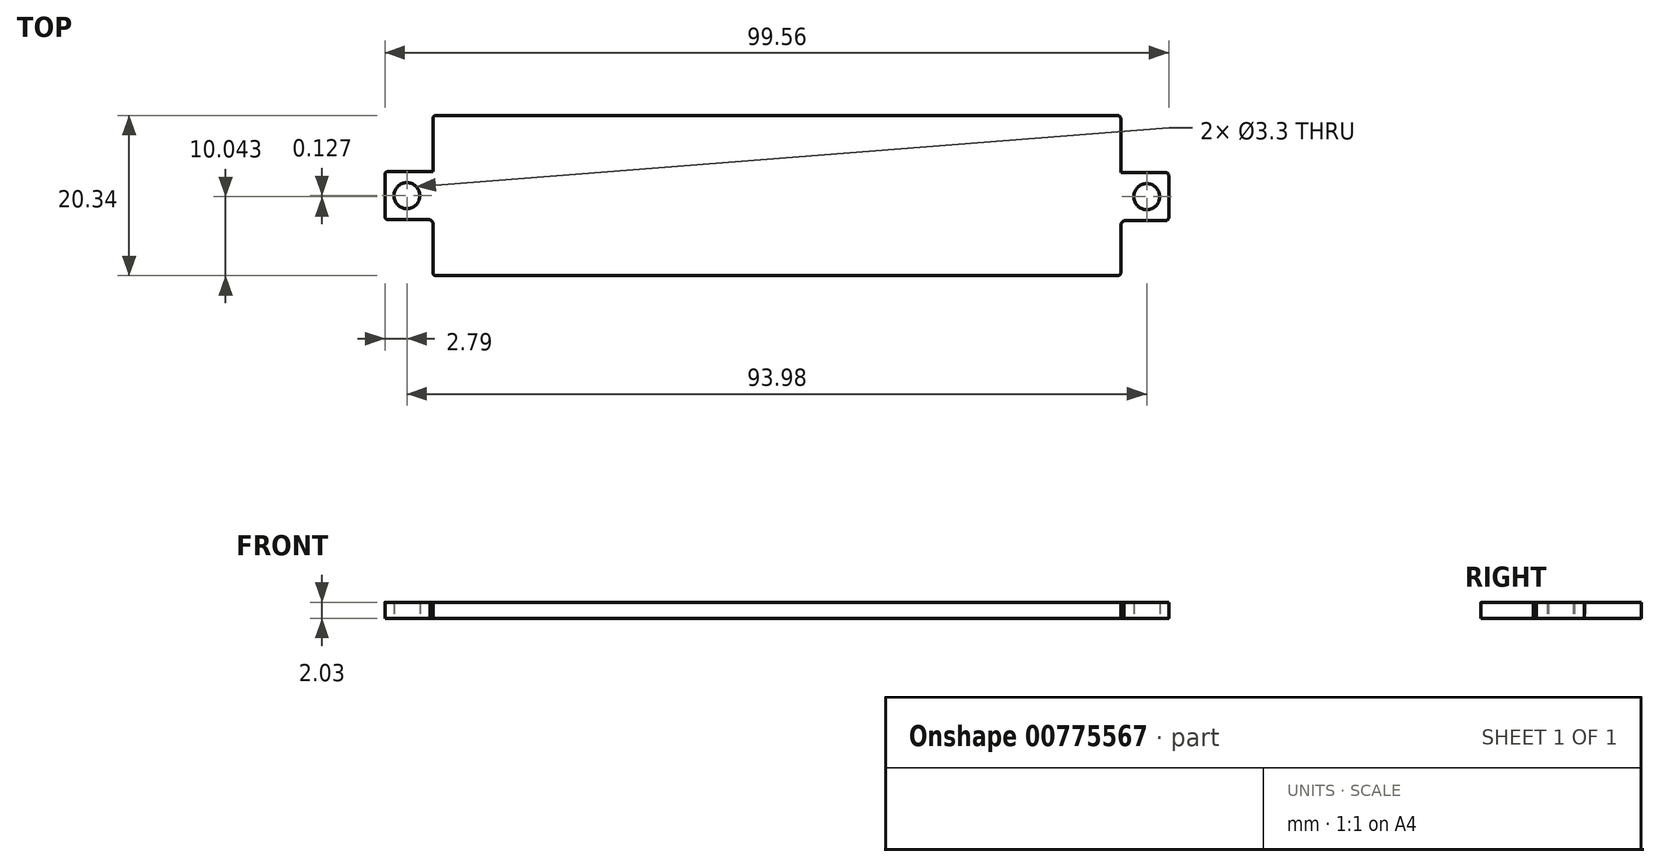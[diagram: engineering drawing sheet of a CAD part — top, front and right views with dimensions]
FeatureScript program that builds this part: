
annotation { "Feature Type Name" : "Feature", "Feature Type Description" : "" }
export const myFeature = defineFeature(function(context is Context, id is Id, definition is map)
    precondition{}
    {
        {
            var Q0;
            Q0=qCreatedBy(makeId("Top.planeOp"),FACE);
            var sketch = newSketch(context, id + "F0", { "sketchPlane" : qUnion([Q0])});
            skLineSegment(sketch, "E0.bottom", {"start": v(43.69, -10.17) * mm, "end": v(-43.69, -10.17) * mm});
            skLineSegment(sketch, "E0.top", {"start": v(43.69, 10.17) * mm, "end": v(-43.69, 10.17) * mm});
            skLineSegment(sketch, "E0.left", {"start": v(43.69, -10.17) * mm, "end": v(43.69, 10.17) * mm});
            skLineSegment(sketch, "E0.right", {"start": v(-43.69, -10.17) * mm, "end": v(-43.69, 10.17) * mm});
            skPoint(sketch, "E0.middle", {"position": v(0, 0) * mm});
            skLineSegment(sketch, "E1.bottom", {"start": v(-43.69, -3.05) * mm, "end": v(-49.78, -3.05) * mm});
            skLineSegment(sketch, "E1.top", {"start": v(-43.69, 3.05) * mm, "end": v(-49.78, 3.05) * mm});
            skLineSegment(sketch, "E1.left", {"start": v(-43.69, -3.05) * mm, "end": v(-43.69, 3.05) * mm});
            skLineSegment(sketch, "E1.right", {"start": v(-49.78, -3.05) * mm, "end": v(-49.78, 3.05) * mm});
            skCircle(sketch, "E2", {"center": v(-47, 0) * mm, "radius": 1.65 * mm});
            skLineSegment(sketch, "E3.bottom", {"start": v(43.69, 2.92) * mm, "end": v(49.78, 2.92) * mm});
            skLineSegment(sketch, "E3.top", {"start": v(43.69, -3.17) * mm, "end": v(49.78, -3.17) * mm});
            skLineSegment(sketch, "E3.left", {"start": v(43.69, 2.92) * mm, "end": v(43.69, -3.17) * mm});
            skLineSegment(sketch, "E3.right", {"start": v(49.78, 2.92) * mm, "end": v(49.78, -3.17) * mm});
            skCircle(sketch, "E4", {"center": v(47, -0.13) * mm, "radius": 1.65 * mm});
            skSolve(sketch);
        }
        {
            var Q0;
            {var subQ3=sQuery(id+"F0.wireOp",EDGE,"E0.bottom");Q0=makeQuery(id+"F0.imprint","IMPRINT",FACE,{"disambiguationData":[TD([[makeQuery(id+"F0.imprint","IMPRINT",EDGE,{"derivedFrom":subQ3}),-1.0]])]});}
            extrude(context, id + "F1", {"entities" : qUnion([Q0]), "depth" : 2.03 * mm, "offsetDistance" : 25.4 * mm});
        }
        {
            var Q0;
            Q0=makeQuery(id+"F0.imprint","IMPRINT",FACE,{"disambiguationData":[TD([[makeQuery(id+"F0.imprint","IMPRINT",EDGE,{"derivedFrom":sQuery(id+"F0.wireOp",EDGE,"E3.bottom")}),-1.0]])]});
            extrude(context, id + "F2", {"entities" : qUnion([Q0]), "operationType" : NewBodyOperationType.ADD, "depth" : 2.03 * mm, "offsetDistance" : 25.4 * mm});
        }
        {
            var Q0;
            Q0=makeQuery(id+"F0.imprint","IMPRINT",FACE,{"disambiguationData":[TD([[makeQuery(id+"F0.imprint","IMPRINT",EDGE,{"derivedFrom":sQuery(id+"F0.wireOp",EDGE,"E1.bottom")}),-1.0]])]});
            extrude(context, id + "F3", {"entities" : qUnion([Q0]), "operationType" : NewBodyOperationType.ADD, "depth" : 2.03 * mm, "offsetDistance" : 25.4 * mm});
        }
        {
            var Q0;
            Q0=makeQuery(id+"F1.opExtrude","SWEPT_EDGE",EDGE,{"disambiguationData":[OSD([sQuery(id+"F0.wireOp",EDGE,"E0.bottom"),sQuery(id+"F0.wireOp",EDGE,"E0.left")])]});
            var Q1;
            Q1=makeQuery(id+"F1.opExtrude","SWEPT_EDGE",EDGE,{"disambiguationData":[OSD([sQuery(id+"F0.wireOp",EDGE,"E0.top"),sQuery(id+"F0.wireOp",EDGE,"E0.left")])]});
            var Q2;
            Q2=makeQuery(id+"F1.opExtrude","SWEPT_EDGE",EDGE,{"disambiguationData":[OSD([sQuery(id+"F0.wireOp",EDGE,"E0.bottom"),sQuery(id+"F0.wireOp",EDGE,"E0.right")])]});
            var Q3;
            Q3=makeQuery(id+"F1.opExtrude","SWEPT_EDGE",EDGE,{"disambiguationData":[OSD([sQuery(id+"F0.wireOp",EDGE,"E0.top"),sQuery(id+"F0.wireOp",EDGE,"E0.right")])]});
            var Q4;
            Q4=makeQuery(id+"F1.opExtrude","SWEPT_EDGE",EDGE,{"disambiguationData":[OSD([sQuery(id+"F0.wireOp",EDGE,"E1.top"),sQuery(id+"F0.wireOp",EDGE,"E1.right")])]});
            var Q5;
            Q5=makeQuery(id+"F1.opExtrude","SWEPT_EDGE",EDGE,{"disambiguationData":[OSD([sQuery(id+"F0.wireOp",EDGE,"E1.bottom"),sQuery(id+"F0.wireOp",EDGE,"E1.right")])]});
            var Q6;
            Q6=makeQuery(id+"F1.opExtrude","SWEPT_EDGE",EDGE,{"disambiguationData":[OSD([sQuery(id+"F0.wireOp",EDGE,"E3.top"),sQuery(id+"F0.wireOp",EDGE,"E3.right")])]});
            var Q7;
            Q7=makeQuery(id+"F1.opExtrude","SWEPT_EDGE",EDGE,{"disambiguationData":[OSD([sQuery(id+"F0.wireOp",EDGE,"E3.bottom"),sQuery(id+"F0.wireOp",EDGE,"E3.right")])]});
            var Q8;
            Q8=makeQuery(id+"F2.opExtrude","SWEPT_EDGE",EDGE,{"disambiguationData":[OSD([sQuery(id+"F0.wireOp",EDGE,"E3.top"),sQuery(id+"F0.wireOp",EDGE,"E3.right")])]});
            var Q9;
            Q9=makeQuery(id+"F2.opExtrude","SWEPT_EDGE",EDGE,{"disambiguationData":[OSD([sQuery(id+"F0.wireOp",EDGE,"E3.bottom"),sQuery(id+"F0.wireOp",EDGE,"E3.right")])]});
            var Q10;
            Q10=makeQuery(id+"F3.opExtrude","SWEPT_EDGE",EDGE,{"disambiguationData":[OSD([sQuery(id+"F0.wireOp",EDGE,"E1.top"),sQuery(id+"F0.wireOp",EDGE,"E1.right")])]});
            var Q11;
            Q11=makeQuery(id+"F3.opExtrude","SWEPT_EDGE",EDGE,{"disambiguationData":[OSD([sQuery(id+"F0.wireOp",EDGE,"E1.bottom"),sQuery(id+"F0.wireOp",EDGE,"E1.right")])]});
            fillet(context, id + "F4", {"entities" : qUnion([Q0, Q1, Q2, Q3, Q4, Q5, Q6, Q7, Q8, Q9, Q10, Q11]), "radius" : 0.38 * mm, "tangentPropagation" : true, "allowEdgeOverflow" : false});
        }
        {
            var Q0;
            Q0=makeQuery(id+"F1.opExtrude","SWEPT_EDGE",EDGE,{"disambiguationData":[OSD([sQuery(id+"F0.wireOp",EDGE,"E0.left"),sQuery(id+"F0.wireOp",EDGE,"E3.bottom"),sQuery(id+"F0.wireOp",EDGE,"E3.left")])]});
            var Q1;
            Q1=makeQuery(id+"F1.opExtrude","SWEPT_EDGE",EDGE,{"disambiguationData":[OSD([sQuery(id+"F0.wireOp",EDGE,"E0.left"),sQuery(id+"F0.wireOp",EDGE,"E3.top"),sQuery(id+"F0.wireOp",EDGE,"E3.left")])]});
            var Q2;
            Q2=makeQuery(id+"F1.opExtrude","SWEPT_EDGE",EDGE,{"disambiguationData":[OSD([sQuery(id+"F0.wireOp",EDGE,"E0.right"),sQuery(id+"F0.wireOp",EDGE,"E1.bottom"),sQuery(id+"F0.wireOp",EDGE,"E1.left")])]});
            var Q3;
            Q3=makeQuery(id+"F1.opExtrude","SWEPT_EDGE",EDGE,{"disambiguationData":[OSD([sQuery(id+"F0.wireOp",EDGE,"E0.right"),sQuery(id+"F0.wireOp",EDGE,"E1.top"),sQuery(id+"F0.wireOp",EDGE,"E1.left")])]});
            var Q4;
            Q4=makeQuery(id+"F3.opExtrude","SWEPT_EDGE",EDGE,{"disambiguationData":[OSD([sQuery(id+"F0.wireOp",EDGE,"E0.right"),sQuery(id+"F0.wireOp",EDGE,"E1.bottom"),sQuery(id+"F0.wireOp",EDGE,"E1.left")])]});
            var Q5;
            Q5=makeQuery(id+"F3.opExtrude","SWEPT_EDGE",EDGE,{"disambiguationData":[OSD([sQuery(id+"F0.wireOp",EDGE,"E0.right"),sQuery(id+"F0.wireOp",EDGE,"E1.top"),sQuery(id+"F0.wireOp",EDGE,"E1.left")])]});
            var Q6;
            Q6=makeQuery(id+"F2.opExtrude","SWEPT_EDGE",EDGE,{"disambiguationData":[OSD([sQuery(id+"F0.wireOp",EDGE,"E0.left"),sQuery(id+"F0.wireOp",EDGE,"E3.bottom"),sQuery(id+"F0.wireOp",EDGE,"E3.left")])]});
            var Q7;
            Q7=makeQuery(id+"F2.opExtrude","SWEPT_EDGE",EDGE,{"disambiguationData":[OSD([sQuery(id+"F0.wireOp",EDGE,"E0.left"),sQuery(id+"F0.wireOp",EDGE,"E3.top"),sQuery(id+"F0.wireOp",EDGE,"E3.left")])]});
            chamfer(context, id + "F5", {"entities" : qUnion([Q0, Q1, Q2, Q3, Q4, Q5, Q6, Q7]), "width" : 0.38 * mm, "tangentPropagation" : true});
        }
    });
